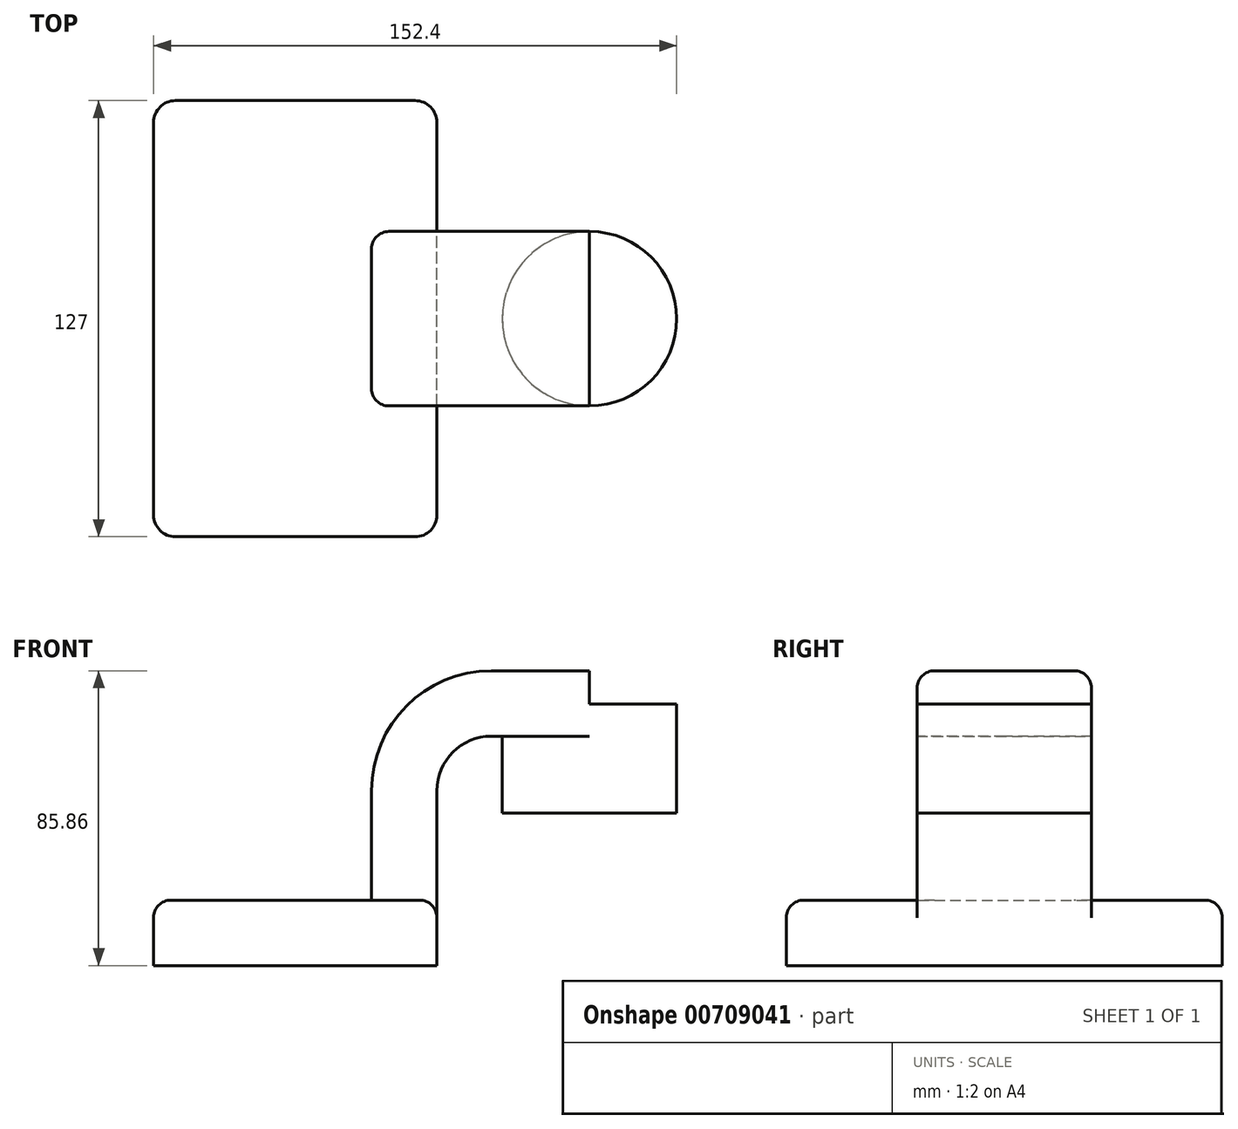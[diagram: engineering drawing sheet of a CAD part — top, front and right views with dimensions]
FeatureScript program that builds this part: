
annotation { "Feature Type Name" : "Feature", "Feature Type Description" : "" }
export const myFeature = defineFeature(function(context is Context, id is Id, definition is map)
    precondition{}
    {
        {
            var Q0;
            Q0=qCreatedBy(makeId("Front.planeOp"),FACE);
            var sketch = newSketch(context, id + "F0", { "sketchPlane" : qUnion([Q0])});
            skLineSegment(sketch, "E0.bottom", {"start": v(-41.28, -9.53) * mm, "end": v(41.28, -9.53) * mm});
            skLineSegment(sketch, "E0.top", {"start": v(-41.28, 9.53) * mm, "end": v(41.28, 9.53) * mm});
            skLineSegment(sketch, "E0.left", {"start": v(-41.28, -9.53) * mm, "end": v(-41.28, 9.53) * mm});
            skLineSegment(sketch, "E0.right", {"start": v(41.28, -9.53) * mm, "end": v(41.28, 9.53) * mm});
            skPoint(sketch, "E0.middle", {"position": v(0, 0) * mm});
            skLineSegment(sketch, "E1.bottom", {"start": v(60.32, 34.93) * mm, "end": v(111.12, 34.93) * mm});
            skLineSegment(sketch, "E1.top", {"start": v(60.32, 66.67) * mm, "end": v(111.12, 66.67) * mm});
            skLineSegment(sketch, "E1.left", {"start": v(60.32, 34.93) * mm, "end": v(60.32, 66.67) * mm});
            skLineSegment(sketch, "E1.right", {"start": v(111.12, 34.93) * mm, "end": v(111.12, 66.67) * mm});
            skPoint(sketch, "E1.middle", {"position": v(85.72, 50.8) * mm});
            skLineSegment(sketch, "E2", {"start": v(41.28, 9.53) * mm, "end": v(41.28, 41.4) * mm});
            skArc(sketch, "E3", {"start": v(41.28, 41.4) * mm, "mid": v(45.92, 52.63) * mm, "end": v(57.15, 57.28) * mm});
            skLineSegment(sketch, "E4", {"start": v(57.15, 57.28) * mm, "end": v(85.72, 57.28) * mm});
            skLineSegment(sketch, "E5.0", {"start": v(57.15, 76.33) * mm, "end": v(85.72, 76.33) * mm});
            skArc(sketch, "E5.1", {"start": v(22.23, 41.4) * mm, "mid": v(32.45, 66.1) * mm, "end": v(57.15, 76.33) * mm});
            skLineSegment(sketch, "E5.2", {"start": v(22.23, 9.53) * mm, "end": v(22.23, 41.4) * mm});
            skLineSegment(sketch, "E6", {"start": v(85.72, 34.93) * mm, "end": v(85.72, 76.33) * mm});
            skFitSpline(sketch, "E7", {"points": [v(-41.28, 9.53) * mm, v(57.15, 76.33) * mm], "startDerivative": vector(1.03, 118.6) * mm, "endDerivative": vector(171.45, -19.2) * mm});
            skSolve(sketch);
        }
        {
            var Q0;
            Q0=makeQuery(id+"F0.imprint","IMPRINT",FACE,{"disambiguationData":[TD([[makeQuery(id+"F0.imprint","IMPRINT",EDGE,{"derivedFrom":sQuery(id+"F0.wireOp",EDGE,"E0.bottom")}),1.0]])]});
            extrude(context, id + "F1", {"entities" : qUnion([Q0]), "endBound" : BoundingType.SYMMETRIC, "depth" : 127 * mm, "offsetDistance" : 25.4 * mm});
        }
        {
            var Q0;
            {var subQ8=sQuery(id+"F0.wireOp",EDGE,"E2");Q0=makeQuery(id+"F0.imprint","IMPRINT",FACE,{"disambiguationData":[TD([[makeQuery(id+"F0.imprint","IMPRINT",EDGE,{"derivedFrom":subQ8}),1.0]])]});}
            var Q1;
            {var subQ0=sQuery(id+"F0.wireOp",EDGE,"E1.left");var subQ1=sQuery(id+"F0.wireOp",EDGE,"E1.top");var subQ2=makeQuery(id+"F0.imprint","INTERSECT",VERTEX,{"derivedFrom":[subQ1,subQ0]});Q1=makeQuery(id+"F0.imprint","IMPRINT",FACE,{"disambiguationData":[TD([[makeQuery(id+"F0.imprint","IMPRINT",EDGE,{"disambiguationData":[TD([[subQ2,-1.0]])],"derivedFrom":subQ1}),-1.0]])]});}
            extrude(context, id + "F2", {"entities" : qUnion([Q0, Q1]), "operationType" : NewBodyOperationType.ADD, "endBound" : BoundingType.SYMMETRIC, "depth" : 50.8 * mm, "offsetDistance" : 25.4 * mm});
        }
        {
            var Q0;
            Q0=makeQuery(id+"F0.imprint","IMPRINT",FACE,{"disambiguationData":[TD([[makeQuery(id+"F0.imprint","IMPRINT",EDGE,{"derivedFrom":sQuery(id+"F0.wireOp",EDGE,"E5.1")}),1.0]])]});
            extrude(context, id + "F3", {"entities" : qUnion([Q0]), "operationType" : NewBodyOperationType.ADD, "endBound" : BoundingType.SYMMETRIC, "depth" : 15.88 * mm, "offsetDistance" : 25.4 * mm});
        }
        {
            var Q0;
            {var subQ4=sQuery(id+"F0.wireOp",EDGE,"E1.right");Q0=makeQuery(id+"F0.imprint","IMPRINT",FACE,{"disambiguationData":[TD([[makeQuery(id+"F0.imprint","IMPRINT",EDGE,{"derivedFrom":subQ4}),1.0]])]});}
            var Q1;
            Q1=sQuery(id+"F0.wireOp",EDGE,"E6");
            revolve(context, id + "F4", {"operationType" : NewBodyOperationType.ADD, "entities" : qUnion([Q0]), "axis" : qUnion([Q1]), "revolveType" : RevolveType.FULL});
        }
        {
            var Q0;
            Q0=makeQuery(id+"F1.opExtrude","CAP_EDGE",EDGE,{"disambiguationData":[OSD([sQuery(id+"F0.wireOp",EDGE,"E0.right")])],"isStart":true});
            var Q1;
            Q1=makeQuery(id+"F1.opExtrude","CAP_EDGE",EDGE,{"disambiguationData":[OSD([sQuery(id+"F0.wireOp",EDGE,"E0.left")])],"isStart":true});
            var Q2;
            Q2=makeQuery(id+"F1.opExtrude","CAP_EDGE",EDGE,{"disambiguationData":[OSD([sQuery(id+"F0.wireOp",EDGE,"E0.left")])],"isStart":false});
            var Q3;
            Q3=makeQuery(id+"F1.opExtrude","CAP_EDGE",EDGE,{"disambiguationData":[OSD([sQuery(id+"F0.wireOp",EDGE,"E0.right")])],"isStart":false});
            fillet(context, id + "F5", {"entities" : qUnion([Q0, Q1, Q2, Q3]), "radius" : 6.35 * mm, "tangentPropagation" : true, "allowEdgeOverflow" : false});
        }
        {
            var Q0;
            Q0=makeQuery(id+"F2.opExtrude","CAP_EDGE",EDGE,{"disambiguationData":[OSD([sQuery(id+"F0.wireOp",EDGE,"E5.0")])],"isStart":true});
            var Q1;
            Q1=makeQuery(id+"F2.opExtrude","CAP_EDGE",EDGE,{"disambiguationData":[OSD([sQuery(id+"F0.wireOp",EDGE,"E5.0")])],"isStart":false});
            var Q2;
            Q2=makeQuery(id+"F1.opExtrude","CAP_EDGE",EDGE,{"disambiguationData":[OSD([sQuery(id+"F0.wireOp",EDGE,"E0.top")])],"isStart":false});
            var Q3;
            Q3=makeQuery(id+"F1.opExtrude","CAP_EDGE",EDGE,{"disambiguationData":[OSD([sQuery(id+"F0.wireOp",EDGE,"E0.top")])],"isStart":true});
            fillet(context, id + "F6", {"entities" : qUnion([Q0, Q1, Q2, Q3]), "radius" : 5.08 * mm, "tangentPropagation" : true, "allowEdgeOverflow" : false});
        }
    });
